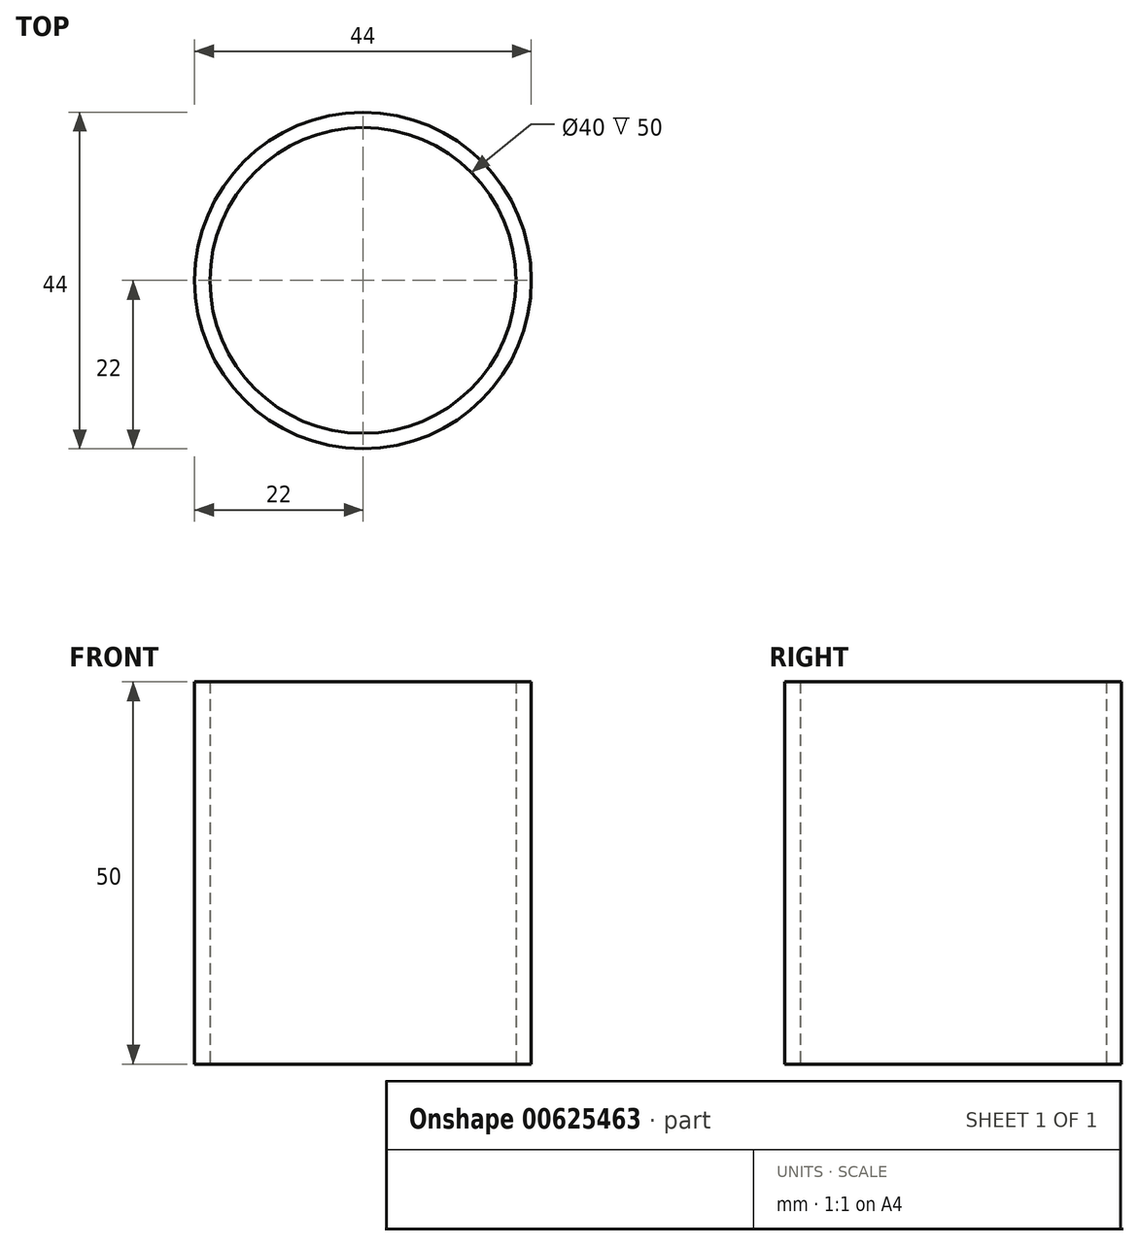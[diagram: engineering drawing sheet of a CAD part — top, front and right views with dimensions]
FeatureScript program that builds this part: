
annotation { "Feature Type Name" : "Feature", "Feature Type Description" : "" }
export const myFeature = defineFeature(function(context is Context, id is Id, definition is map)
    precondition{}
    {
        {
            var Q0;
            Q0=qCreatedBy(makeId("Front.planeOp"),FACE);
            var sketch = newSketch(context, id + "F0", { "sketchPlane" : qUnion([Q0])});
            skLineSegment(sketch, "E0.bottom", {"start": v(-22, 50) * mm, "end": v(0, 50) * mm});
            skLineSegment(sketch, "E0.top", {"start": v(-22, 0) * mm, "end": v(0, 0) * mm});
            skLineSegment(sketch, "E0.left", {"start": v(-22, 50) * mm, "end": v(-22, 0) * mm});
            skLineSegment(sketch, "E0.right", {"start": v(0, 50) * mm, "end": v(0, 0) * mm});
            skSolve(sketch);
        }
        {
            var Q0;
            Q0=makeQuery(id+"F0.imprint","IMPRINT",FACE,{"disambiguationData":[TD([[makeQuery(id+"F0.imprint","IMPRINT",EDGE,{"derivedFrom":sQuery(id+"F0.wireOp",EDGE,"E0.bottom")}),-1.0]])]});
            var Q1;
            Q1=sQuery(id+"F0.wireOp",EDGE,"E0.right");
            revolve(context, id + "F1", {"entities" : qUnion([Q0]), "axis" : qUnion([Q1]), "revolveType" : RevolveType.FULL});
        }
        {
            var Q0;
            Q0=qCreatedBy(makeId("Front.planeOp"),FACE);
            var sketch = newSketch(context, id + "F2", { "sketchPlane" : qUnion([Q0])});
            skLineSegment(sketch, "E1.bottom", {"start": v(-20, 50) * mm, "end": v(0, 50) * mm});
            skLineSegment(sketch, "E1.top", {"start": v(-20, 0) * mm, "end": v(0, 0) * mm});
            skLineSegment(sketch, "E1.left", {"start": v(-20, 50) * mm, "end": v(-20, 0) * mm});
            skLineSegment(sketch, "E1.right", {"start": v(0, 50) * mm, "end": v(0, 0) * mm});
            skSolve(sketch);
        }
        {
            var Q0;
            Q0 = qSketchRegion(id + "F2", true);
            var Q1;
            Q1=sQuery(id+"F2.wireOp",EDGE,"E1.right");
            revolve(context, id + "F3", {"operationType" : NewBodyOperationType.REMOVE, "entities" : qUnion([Q0]), "axis" : qUnion([Q1]), "revolveType" : RevolveType.FULL, "oppositeDirection" : true});
        }
    });
